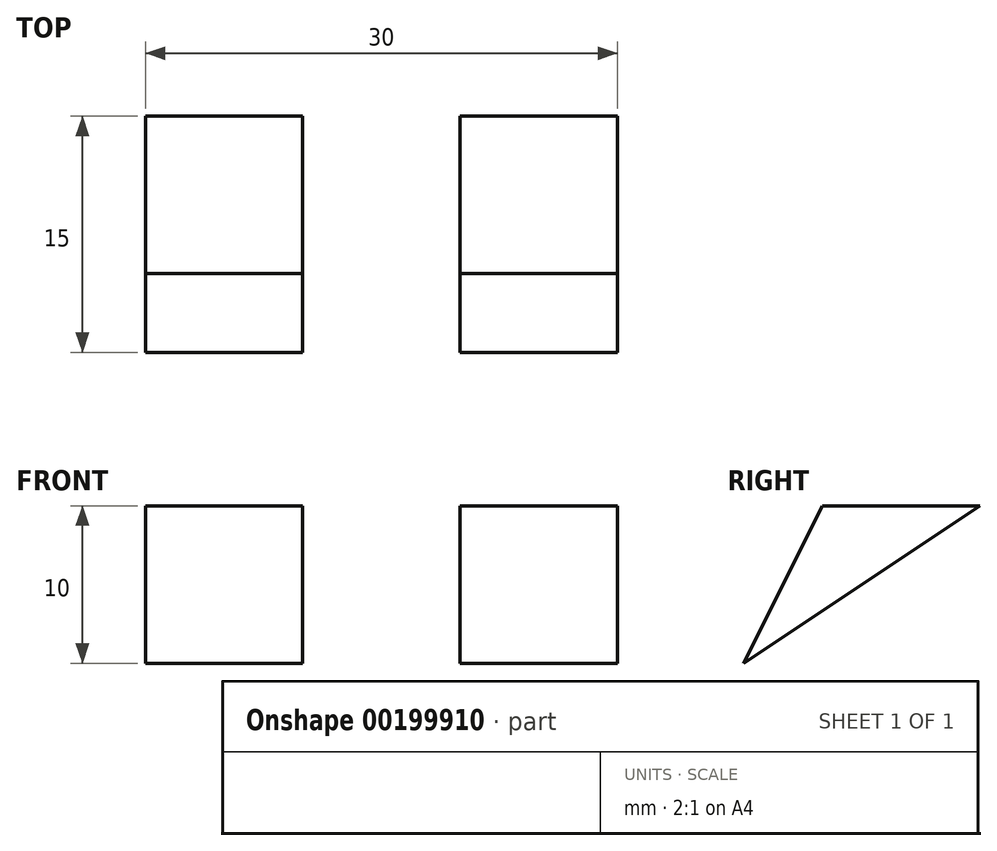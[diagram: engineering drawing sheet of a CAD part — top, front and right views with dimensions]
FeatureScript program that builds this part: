
annotation { "Feature Type Name" : "Feature", "Feature Type Description" : "" }
export const myFeature = defineFeature(function(context is Context, id is Id, definition is map)
    precondition{}
    {
        {
            var Q0;
            Q0=qCreatedBy(makeId("Right.planeOp"),FACE);
            var sketch = newSketch(context, id + "F0", { "sketchPlane" : qUnion([Q0])});
            skLineSegment(sketch, "E0", {"start": v(0, 0) * mm, "end": v(-15, 0) * mm});
            skLineSegment(sketch, "E1", {"start": v(-15, 0) * mm, "end": v(0, 0) * mm});
            skLineSegment(sketch, "E2", {"start": v(0, 20) * mm, "end": v(0, 0) * mm});
            skLineSegment(sketch, "E3", {"start": v(0, 20) * mm, "end": v(-10, 20) * mm});
            skLineSegment(sketch, "E4", {"start": v(-15, 10) * mm, "end": v(-10, 20) * mm});
            skLineSegment(sketch, "E5", {"start": v(-15, 10) * mm, "end": v(-20, 10) * mm});
            skLineSegment(sketch, "E6", {"start": v(-20, 10) * mm, "end": v(-20, 5) * mm});
            skLineSegment(sketch, "E7", {"start": v(-20, 5) * mm, "end": v(-15, 0) * mm});
            skLineSegment(sketch, "E8", {"start": v(-15, 10) * mm, "end": v(0, 20) * mm});
            skSolve(sketch);
        }
        {
            var Q0;
            Q0=makeQuery(id+"F0.imprint","IMPRINT",FACE,{"disambiguationData":[TD([[makeQuery(id+"F0.imprint","IMPRINT",EDGE,{"derivedFrom":sQuery(id+"F0.wireOp",EDGE,"E1")}),1.0]])]});
            var Q1;
            Q1=makeQuery(id+"F0.imprint","IMPRINT",FACE,{"disambiguationData":[TD([[makeQuery(id+"F0.imprint","IMPRINT",EDGE,{"derivedFrom":sQuery(id+"F0.wireOp",EDGE,"E3")}),1.0]])]});
            extrude(context, id + "F1", {"entities" : qUnion([Q0, Q1]), "depth" : 15 * mm});
        }
        {
            var Q0;
            Q0=makeQuery(id+"F0.imprint","IMPRINT",FACE,{"disambiguationData":[TD([[makeQuery(id+"F0.imprint","IMPRINT",EDGE,{"derivedFrom":sQuery(id+"F0.wireOp",EDGE,"E3")}),1.0]])]});
            extrude(context, id + "F2", {"entities" : qUnion([Q0]), "operationType" : NewBodyOperationType.REMOVE, "depth" : 5 * mm});
        }
        {
            var Q0;
            Q0=makeQuery(id+"F1.opExtrude","SWEPT_BODY",BODY,{"disambiguationData":[OSD([sQuery(id+"F0.wireOp",EDGE,"E1"),sQuery(id+"F0.wireOp",EDGE,"E2"),sQuery(id+"F0.wireOp",EDGE,"E3"),sQuery(id+"F0.wireOp",EDGE,"E4"),sQuery(id+"F0.wireOp",EDGE,"E5"),sQuery(id+"F0.wireOp",EDGE,"E6"),sQuery(id+"F0.wireOp",EDGE,"E7")])]});
            var Q1;
            Q1=makeQuery(id+"F0.imprint","IMPRINT",FACE,{"disambiguationData":[TD([[makeQuery(id+"F0.imprint","IMPRINT",EDGE,{"derivedFrom":sQuery(id+"F0.wireOp",EDGE,"E3")}),1.0]])]});
            mirror(context, id + "F3", {"operationType" : NewBodyOperationType.ADD, "entities" : qUnion([Q0]), "mirrorPlane" : qUnion([Q1])});
        }
    });
